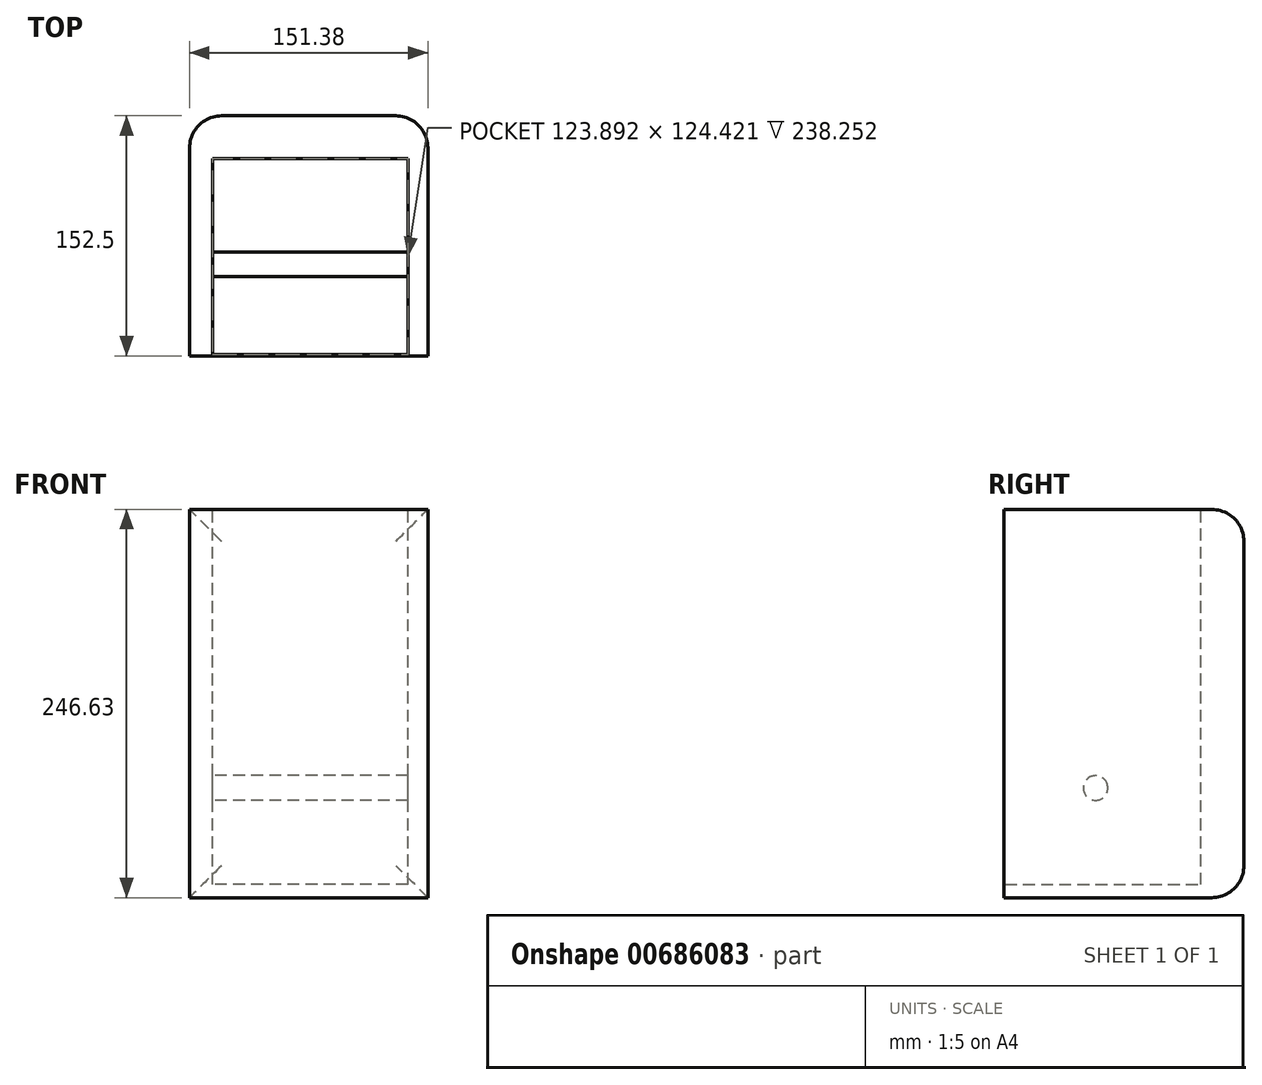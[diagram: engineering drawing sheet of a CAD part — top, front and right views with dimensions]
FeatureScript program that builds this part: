
annotation { "Feature Type Name" : "Feature", "Feature Type Description" : "" }
export const myFeature = defineFeature(function(context is Context, id is Id, definition is map)
    precondition{}
    {
        {
            var Q0;
            Q0=qCreatedBy(makeId("Top.planeOp"),FACE);
            cPlane(context, id + "F0", {"entities" : qUnion([Q0]), "cplaneType" : CPlaneType.OFFSET, "offset" : 76.45 * mm, "oppositeDirection" : true, "width" : 152.4 * mm, "height" : 152.4 * mm});
        }
        {
            var Q0;
            Q0=qCreatedBy(id+"F0.planeOp",FACE);
            var sketch = newSketch(context, id + "F1", { "sketchPlane" : qUnion([Q0])});
            skLineSegment(sketch, "E0.bottom", {"start": v(-75.7, -76.04) * mm, "end": v(75.7, -76.04) * mm});
            skLineSegment(sketch, "E0.top", {"start": v(-75.7, 75.7) * mm, "end": v(75.7, 75.7) * mm});
            skLineSegment(sketch, "E0.left", {"start": v(-75.7, -76.04) * mm, "end": v(-75.7, 75.7) * mm});
            skLineSegment(sketch, "E0.right", {"start": v(75.7, -76.04) * mm, "end": v(75.7, 75.7) * mm});
            skSolve(sketch);
        }
        {
            var Q0;
            Q0 = qSketchRegion(id + "F1", true);
            extrude(context, id + "F2", {"entities" : qUnion([Q0]), "depth" : 246.63 * mm, "offsetDistance" : 25.4 * mm});
        }
        {
            var Q0;
            Q0=makeQuery(id+"F2.opExtrude","CAP_EDGE",EDGE,{"disambiguationData":[OSD([sQuery(id+"F1.wireOp",EDGE,"E0.top")])],"isStart":false});
            var Q1;
            Q1=makeQuery(id+"F2.opExtrude","SWEPT_EDGE",EDGE,{"disambiguationData":[OSD([sQuery(id+"F1.wireOp",EDGE,"E0.top"),sQuery(id+"F1.wireOp",EDGE,"E0.right")])]});
            var Q2;
            Q2=makeQuery(id+"F2.opExtrude","CAP_EDGE",EDGE,{"disambiguationData":[OSD([sQuery(id+"F1.wireOp",EDGE,"E0.top")])],"isStart":true});
            var Q3;
            Q3=makeQuery(id+"F2.opExtrude","SWEPT_FACE",FACE,{"disambiguationData":[OSD([sQuery(id+"F1.wireOp",EDGE,"E0.top")])]});
            fillet(context, id + "F3", {"entities" : qUnion([Q0, Q1, Q2, Q3]), "radius" : 20.32 * mm, "tangentPropagation" : true, "allowEdgeOverflow" : false});
        }
        {
            var Q0;
            Q0=makeQuery(id+"F2.opExtrude","CAP_FACE",FACE,{"disambiguationData":[OSD([sQuery(id+"F1.wireOp",EDGE,"E0.bottom"),sQuery(id+"F1.wireOp",EDGE,"E0.top"),sQuery(id+"F1.wireOp",EDGE,"E0.left"),sQuery(id+"F1.wireOp",EDGE,"E0.right")])],"isStart":false});
            var sketch = newSketch(context, id + "F4", { "sketchPlane" : qUnion([Q0])});
            skLineSegment(sketch, "E1.bottom", {"start": v(63, -76.04) * mm, "end": v(-60.89, -76.04) * mm});
            skLineSegment(sketch, "E1.top", {"start": v(63, 48.38) * mm, "end": v(-60.89, 48.38) * mm});
            skLineSegment(sketch, "E1.left", {"start": v(63, -76.04) * mm, "end": v(63, 48.38) * mm});
            skLineSegment(sketch, "E1.right", {"start": v(-60.89, -76.04) * mm, "end": v(-60.89, 48.38) * mm});
            skSolve(sketch);
        }
        {
            var Q0;
            Q0 = qSketchRegion(id + "F4", true);
            extrude(context, id + "F5", {"entities" : qUnion([Q0]), "operationType" : NewBodyOperationType.REMOVE, "oppositeDirection" : true, "depth" : 238.25 * mm, "offsetDistance" : 25.4 * mm});
        }
        {
            var Q0;
            Q0=makeQuery(id+"F2.opExtrude","SWEPT_FACE",FACE,{"disambiguationData":[OSD([sQuery(id+"F1.wireOp",EDGE,"E0.bottom")])]});
            var sketch = newSketch(context, id + "F6", { "sketchPlane" : qUnion([Q0])});
            skLineSegment(sketch, "E2.bottom", {"start": v(-75.7, 170.18) * mm, "end": v(75.7, 170.18) * mm});
            skLineSegment(sketch, "E2.top", {"start": v(-75.7, -76.45) * mm, "end": v(75.7, -76.45) * mm});
            skLineSegment(sketch, "E2.left", {"start": v(-75.7, 170.18) * mm, "end": v(-75.7, -76.45) * mm});
            skLineSegment(sketch, "E2.right", {"start": v(75.7, 170.18) * mm, "end": v(75.7, -76.45) * mm});
            skSolve(sketch);
        }
        {
            var Q0;
            Q0 = qSketchRegion(id + "F6", true);
            extrude(context, id + "F7", {"entities" : qUnion([Q0]), "operationType" : NewBodyOperationType.ADD, "depth" : 0.76 * mm, "offsetDistance" : 25.4 * mm});
        }
        {
            var Q0;
            Q0=makeQuery(id+"F5.boolean.opBoolean","COPY",FACE,{"derivedFrom":makeQuery(id+"F5.opExtrude","SWEPT_FACE",FACE,{"disambiguationData":[OSD([sQuery(id+"F4.wireOp",EDGE,"E1.right")])]})});
            var sketch = newSketch(context, id + "F8", { "sketchPlane" : qUnion([Q0])});
            skCircle(sketch, "E3", {"center": v(-18.55, -6.75) * mm, "radius": 7.82 * mm});
            skSolve(sketch);
        }
        {
            var Q0;
            Q0 = qSketchRegion(id + "F8", true);
            extrude(context, id + "F9", {"entities" : qUnion([Q0]), "operationType" : NewBodyOperationType.ADD, "depth" : 130.3 * mm, "offsetDistance" : 25.4 * mm});
        }
    });
